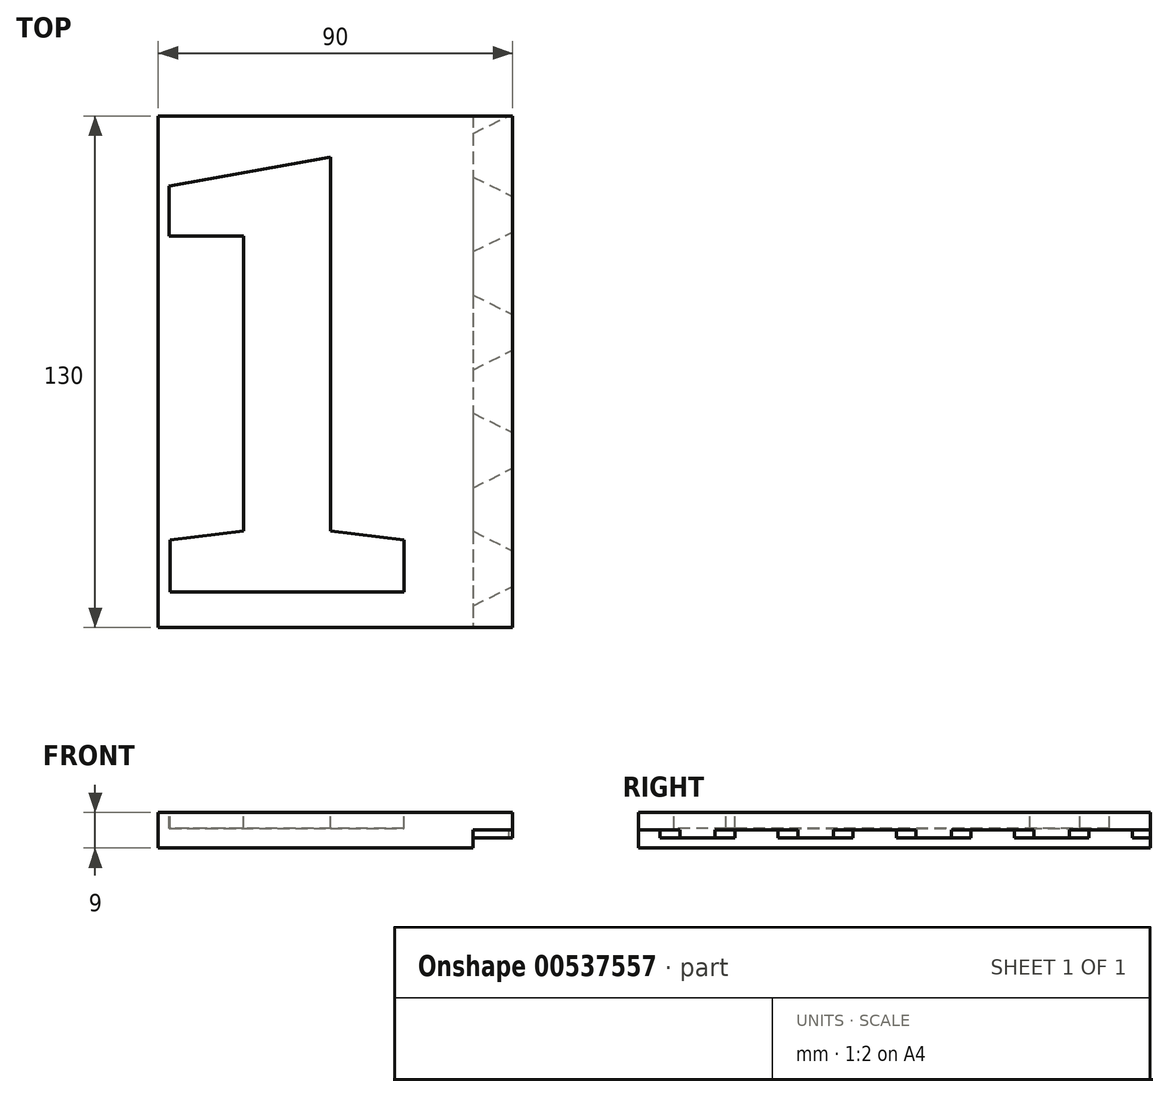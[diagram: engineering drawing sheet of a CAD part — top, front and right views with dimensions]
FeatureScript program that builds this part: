
annotation { "Feature Type Name" : "Feature", "Feature Type Description" : "" }
export const myFeature = defineFeature(function(context is Context, id is Id, definition is map)
    precondition{}
    {
        {
            var Q0;
            Q0=qCreatedBy(makeId("Top.planeOp"),FACE);
            var sketch = newSketch(context, id + "F0", { "sketchPlane" : qUnion([Q0])});
            skLineSegment(sketch, "E0.bottom", {"start": v(45, -65) * mm, "end": v(-45, -65) * mm});
            skLineSegment(sketch, "E0.top", {"start": v(45, 65) * mm, "end": v(-45, 65) * mm});
            skLineSegment(sketch, "E0.left", {"start": v(45, -65) * mm, "end": v(45, 65) * mm});
            skLineSegment(sketch, "E0.right", {"start": v(-45, -65) * mm, "end": v(-45, 65) * mm});
            skPoint(sketch, "E0.middle", {"position": v(0, 0) * mm});
            skSolve(sketch);
        }
        {
            var Q0;
            Q0 = qSketchRegion(id + "F0", true);
            extrude(context, id + "F1", {"entities" : qUnion([Q0]), "depth" : 9 * mm, "offsetDistance" : 25 * mm});
        }
        {
            var Q0;
            Q0=makeQuery(id+"F1.opExtrude","CAP_FACE",FACE,{"disambiguationData":[OSD([sQuery(id+"F0.wireOp",EDGE,"E0.bottom"),sQuery(id+"F0.wireOp",EDGE,"E0.top"),sQuery(id+"F0.wireOp",EDGE,"E0.left"),sQuery(id+"F0.wireOp",EDGE,"E0.right")])],"isStart":false});
            var sketch = newSketch(context, id + "F2", { "sketchPlane" : qUnion([Q0])});
            skLineSegment(sketch, "E1.bottom", {"start": v(-45, 65) * mm, "end": v(35, 65) * mm});
            skLineSegment(sketch, "E1.top", {"start": v(-45, -65) * mm, "end": v(35, -65) * mm});
            skLineSegment(sketch, "E1.left", {"start": v(-45, 65) * mm, "end": v(-45, -65) * mm});
            skLineSegment(sketch, "E1.right", {"start": v(35, 65) * mm, "end": v(35, -65) * mm});
            skText(sketch, "E2", { "text": "1", "fontName": "RobotoSlab-Bold.ttf"});
            skPoint(sketch, "E3", {"position": v(-5, 65) * mm});
            skLineSegment(sketch, "E4", {"start": v(-5, 56) * mm, "end": v(-5, 65) * mm});
            skLineSegment(sketch, "E5", {"start": v(-5, -56) * mm, "end": v(-5, -65) * mm});
            const initialGuessF2  = {"E2": [-0.04697, -0.056, 1, 0, 0.112]};
            skSetInitialGuess(sketch, initialGuessF2);
            skSolve(sketch);
        }
        {
            var Q0;
            Q0=makeQuery(id+"F2.imprint","IMPRINT",FACE,{"disambiguationData":[TD([[makeQuery(id+"F2.imprint","IMPRINT",EDGE,{"derivedFrom":sQuery(id+"F2.wireOp",EDGE,"E2.sketch_text.stroke-0")}),-1.0]])]});
            extrude(context, id + "F3", {"entities" : qUnion([Q0]), "operationType" : NewBodyOperationType.REMOVE, "oppositeDirection" : true, "depth" : 4 * mm, "offsetDistance" : 25 * mm});
        }
        {
            var Q0;
            Q0=makeQuery(id+"F1.opExtrude","CAP_FACE",FACE,{"disambiguationData":[OSD([sQuery(id+"F0.wireOp",EDGE,"E0.bottom"),sQuery(id+"F0.wireOp",EDGE,"E0.top"),sQuery(id+"F0.wireOp",EDGE,"E0.left"),sQuery(id+"F0.wireOp",EDGE,"E0.right")])],"isStart":true});
            var sketch = newSketch(context, id + "F4", { "sketchPlane" : qUnion([Q0])});
            skLineSegment(sketch, "E6.bottom", {"start": v(-45, -65) * mm, "end": v(35, -65) * mm});
            skLineSegment(sketch, "E6.top", {"start": v(-45, 65) * mm, "end": v(35, 65) * mm});
            skLineSegment(sketch, "E6.left", {"start": v(-45, -65) * mm, "end": v(-45, 65) * mm});
            skLineSegment(sketch, "E6.right", {"start": v(35, -65) * mm, "end": v(35, 65) * mm});
            skLineSegment(sketch, "E7", {"start": v(45, -65) * mm, "end": v(45, -45) * mm});
            skLineSegment(sketch, "E8", {"start": v(35, -50) * mm, "end": v(35, -60) * mm});
            skLineSegment(sketch, "E9", {"start": v(45, -65) * mm, "end": v(35, -60) * mm});
            skLineSegment(sketch, "E10", {"start": v(45, -45) * mm, "end": v(35, -50) * mm});
            skLineSegment(sketch, "E11.0.1.0", {"start": v(45, -35) * mm, "end": v(35, -30) * mm});
            skLineSegment(sketch, "E11.0.1.1", {"start": v(45, -35) * mm, "end": v(45, -15) * mm});
            skLineSegment(sketch, "E11.0.1.2", {"start": v(45, -15) * mm, "end": v(35, -20) * mm});
            skLineSegment(sketch, "E11.0.1.3", {"start": v(35, -20) * mm, "end": v(35, -30) * mm});
            skLineSegment(sketch, "E11.0.2.0", {"start": v(45, -5) * mm, "end": v(35, 0) * mm});
            skLineSegment(sketch, "E11.0.2.1", {"start": v(45, -5) * mm, "end": v(45, 15) * mm});
            skLineSegment(sketch, "E11.0.2.2", {"start": v(45, 15) * mm, "end": v(35, 10) * mm});
            skLineSegment(sketch, "E11.0.2.3", {"start": v(35, 10) * mm, "end": v(35, 0) * mm});
            skLineSegment(sketch, "E11.0.3.0", {"start": v(45, 25) * mm, "end": v(35, 30) * mm});
            skLineSegment(sketch, "E11.0.3.1", {"start": v(45, 25) * mm, "end": v(45, 45) * mm});
            skLineSegment(sketch, "E11.0.3.2", {"start": v(45, 45) * mm, "end": v(35, 40) * mm});
            skLineSegment(sketch, "E11.0.3.3", {"start": v(35, 40) * mm, "end": v(35, 30) * mm});
            skLineSegment(sketch, "E11.0.4.0", {"start": v(45, 55) * mm, "end": v(35, 60) * mm});
            skLineSegment(sketch, "E11.0.4.1", {"start": v(45, 55) * mm, "end": v(45, 75) * mm});
            skLineSegment(sketch, "E11.0.4.2", {"start": v(45, 75) * mm, "end": v(35, 70) * mm});
            skLineSegment(sketch, "E11.0.4.3", {"start": v(35, 70) * mm, "end": v(35, 60) * mm});
            skLineSegment(sketch, "E11.direction1", {"start": v(35, -60) * mm, "end": v(55, -60) * mm, "construction": true});
            skLineSegment(sketch, "E11.direction2", {"start": v(35, -60) * mm, "end": v(35, -30) * mm, "construction": true});
            skSolve(sketch);
        }
        {
            var Q0;
            Q0=makeQuery(id+"F4.imprint","IMPRINT",FACE,{"disambiguationData":[TD([[makeQuery(id+"F4.imprint","IMPRINT",EDGE,{"derivedFrom":sQuery(id+"F4.wireOp",EDGE,"E7")}),-1.0]])]});
            var Q1;
            Q1=makeQuery(id+"F4.imprint","IMPRINT",FACE,{"disambiguationData":[TD([[makeQuery(id+"F4.imprint","IMPRINT",EDGE,{"derivedFrom":sQuery(id+"F4.wireOp",EDGE,"E11.0.1.0")}),-1.0]])]});
            var Q2;
            Q2=makeQuery(id+"F4.imprint","IMPRINT",FACE,{"disambiguationData":[TD([[makeQuery(id+"F4.imprint","IMPRINT",EDGE,{"derivedFrom":sQuery(id+"F4.wireOp",EDGE,"E11.0.2.0")}),-1.0]])]});
            var Q3;
            Q3=makeQuery(id+"F4.imprint","IMPRINT",FACE,{"disambiguationData":[TD([[makeQuery(id+"F4.imprint","IMPRINT",EDGE,{"derivedFrom":sQuery(id+"F4.wireOp",EDGE,"E11.0.3.0")}),-1.0]])]});
            var Q4;
            {var subQ0=sQuery(id+"F4.wireOp",EDGE,"E11.0.4.0");Q4=makeQuery(id+"F4.imprint","IMPRINT",FACE,{"disambiguationData":[TD([[makeQuery(id+"F4.imprint","IMPRINT",EDGE,{"derivedFrom":subQ0}),-1.0]])]});}
            extrude(context, id + "F5", {"entities" : qUnion([Q0, Q1, Q2, Q3, Q4]), "operationType" : NewBodyOperationType.REMOVE, "oppositeDirection" : true, "depth" : 4.6 * mm, "offsetDistance" : 25 * mm});
        }
        {
            var Q0;
            {var subQ2=sQuery(id+"F4.wireOp",EDGE,"E11.0.3.2");Q0=makeQuery(id+"F4.imprint","IMPRINT",FACE,{"disambiguationData":[TD([[makeQuery(id+"F4.imprint","IMPRINT",EDGE,{"derivedFrom":subQ2}),-1.0]])]});}
            var Q1;
            {var subQ0=sQuery(id+"F4.wireOp",EDGE,"E11.0.2.2");Q1=makeQuery(id+"F4.imprint","IMPRINT",FACE,{"disambiguationData":[TD([[makeQuery(id+"F4.imprint","IMPRINT",EDGE,{"derivedFrom":subQ0}),-1.0]])]});}
            var Q2;
            {var subQ0=sQuery(id+"F4.wireOp",EDGE,"E11.0.1.2");Q2=makeQuery(id+"F4.imprint","IMPRINT",FACE,{"disambiguationData":[TD([[makeQuery(id+"F4.imprint","IMPRINT",EDGE,{"derivedFrom":subQ0}),-1.0]])]});}
            var Q3;
            {var subQ0=sQuery(id+"F4.wireOp",EDGE,"E10");Q3=makeQuery(id+"F4.imprint","IMPRINT",FACE,{"disambiguationData":[TD([[makeQuery(id+"F4.imprint","IMPRINT",EDGE,{"derivedFrom":subQ0}),-1.0]])]});}
            var Q4;
            {var subQ3=sQuery(id+"F4.wireOp",EDGE,"E9");Q4=makeQuery(id+"F4.imprint","IMPRINT",FACE,{"disambiguationData":[TD([[makeQuery(id+"F4.imprint","IMPRINT",EDGE,{"derivedFrom":subQ3}),1.0]])]});}
            extrude(context, id + "F6", {"entities" : qUnion([Q0, Q1, Q2, Q3, Q4]), "operationType" : NewBodyOperationType.REMOVE, "oppositeDirection" : true, "depth" : 2.6 * mm, "offsetDistance" : 25 * mm});
        }
        {
            var Q0;
            Q0=makeQuery(id+"F6.boolean.opBoolean","COPY",FACE,{"derivedFrom":makeQuery(id+"F6.opExtrude","CAP_FACE",FACE,{"disambiguationData":[OSD([sQuery(id+"F0.wireOp",EDGE,"E0.left"),sQuery(id+"F4.wireOp",EDGE,"E6.right"),sQuery(id+"F4.wireOp",EDGE,"E11.0.3.2"),sQuery(id+"F4.wireOp",EDGE,"E11.0.4.0")])],"isStart":false})});
            var sketch = newSketch(context, id + "F7", { "sketchPlane" : qUnion([Q0])});
            skLineSegment(sketch, "E12", {"start": v(35, 60) * mm, "end": v(35, 59.5) * mm});
            skLineSegment(sketch, "E13", {"start": v(35, 59.5) * mm, "end": v(45, 54.5) * mm});
            skLineSegment(sketch, "E14", {"start": v(45, 54.5) * mm, "end": v(45, 55) * mm});
            skLineSegment(sketch, "E15", {"start": v(45, 55) * mm, "end": v(35, 60) * mm});
            skLineSegment(sketch, "E16", {"start": v(35, 40) * mm, "end": v(35, 40.5) * mm});
            skLineSegment(sketch, "E17", {"start": v(35, 40.5) * mm, "end": v(45, 45.5) * mm});
            skLineSegment(sketch, "E18", {"start": v(45, 45.5) * mm, "end": v(45, 45) * mm});
            skLineSegment(sketch, "E19", {"start": v(35, 40) * mm, "end": v(45, 45) * mm});
            skLineSegment(sketch, "E20.0.1.0", {"start": v(45, 25) * mm, "end": v(35, 30) * mm});
            skLineSegment(sketch, "E20.0.1.1", {"start": v(35, 29.5) * mm, "end": v(45, 24.5) * mm});
            skLineSegment(sketch, "E20.0.1.2", {"start": v(45, 24.5) * mm, "end": v(45, 25) * mm});
            skLineSegment(sketch, "E20.0.1.3", {"start": v(35, 30) * mm, "end": v(35, 29.5) * mm});
            skLineSegment(sketch, "E20.0.1.4", {"start": v(35, 10.5) * mm, "end": v(45, 15.5) * mm});
            skLineSegment(sketch, "E20.0.1.5", {"start": v(35, 10) * mm, "end": v(45, 15) * mm});
            skLineSegment(sketch, "E20.0.1.6", {"start": v(35, 10) * mm, "end": v(35, 10.5) * mm});
            skLineSegment(sketch, "E20.0.1.7", {"start": v(45, 15.5) * mm, "end": v(45, 15) * mm});
            skLineSegment(sketch, "E20.0.2.0", {"start": v(45, -5) * mm, "end": v(35, 0) * mm});
            skLineSegment(sketch, "E20.0.2.1", {"start": v(35, -0.5) * mm, "end": v(45, -5.5) * mm});
            skLineSegment(sketch, "E20.0.2.2", {"start": v(45, -5.5) * mm, "end": v(45, -5) * mm});
            skLineSegment(sketch, "E20.0.2.3", {"start": v(35, 0) * mm, "end": v(35, -0.5) * mm});
            skLineSegment(sketch, "E20.0.2.4", {"start": v(35, -19.5) * mm, "end": v(45, -14.5) * mm});
            skLineSegment(sketch, "E20.0.2.5", {"start": v(35, -20) * mm, "end": v(45, -15) * mm});
            skLineSegment(sketch, "E20.0.2.6", {"start": v(35, -20) * mm, "end": v(35, -19.5) * mm});
            skLineSegment(sketch, "E20.0.2.7", {"start": v(45, -14.5) * mm, "end": v(45, -15) * mm});
            skLineSegment(sketch, "E20.0.3.0", {"start": v(45, -35) * mm, "end": v(35, -30) * mm});
            skLineSegment(sketch, "E20.0.3.1", {"start": v(35, -30.5) * mm, "end": v(45, -35.5) * mm});
            skLineSegment(sketch, "E20.0.3.2", {"start": v(45, -35.5) * mm, "end": v(45, -35) * mm});
            skLineSegment(sketch, "E20.0.3.3", {"start": v(35, -30) * mm, "end": v(35, -30.5) * mm});
            skLineSegment(sketch, "E20.0.3.4", {"start": v(35, -49.5) * mm, "end": v(45, -44.5) * mm});
            skLineSegment(sketch, "E20.0.3.5", {"start": v(35, -50) * mm, "end": v(45, -45) * mm});
            skLineSegment(sketch, "E20.0.3.6", {"start": v(35, -50) * mm, "end": v(35, -49.5) * mm});
            skLineSegment(sketch, "E20.0.3.7", {"start": v(45, -44.5) * mm, "end": v(45, -45) * mm});
            skLineSegment(sketch, "E20.0.4.0", {"start": v(45, -65) * mm, "end": v(35, -60) * mm});
            skLineSegment(sketch, "E20.0.4.1", {"start": v(35, -60.5) * mm, "end": v(45, -65.5) * mm});
            skLineSegment(sketch, "E20.0.4.2", {"start": v(45, -65.5) * mm, "end": v(45, -65) * mm});
            skLineSegment(sketch, "E20.0.4.3", {"start": v(35, -60) * mm, "end": v(35, -60.5) * mm});
            skLineSegment(sketch, "E20.0.4.4", {"start": v(35, -79.5) * mm, "end": v(45, -74.5) * mm});
            skLineSegment(sketch, "E20.0.4.5", {"start": v(35, -80) * mm, "end": v(45, -75) * mm});
            skLineSegment(sketch, "E20.0.4.6", {"start": v(35, -80) * mm, "end": v(35, -79.5) * mm});
            skLineSegment(sketch, "E20.0.4.7", {"start": v(45, -74.5) * mm, "end": v(45, -75) * mm});
            skLineSegment(sketch, "E20.direction1", {"start": v(35, 60) * mm, "end": v(60, 60) * mm, "construction": true});
            skLineSegment(sketch, "E20.direction2", {"start": v(35, 60) * mm, "end": v(35, 30) * mm, "construction": true});
            skSolve(sketch);
        }
        {
            var Q0;
            Q0 = qSketchRegion(id + "F7", true);
            extrude(context, id + "F8", {"entities" : qUnion([Q0]), "operationType" : NewBodyOperationType.REMOVE, "oppositeDirection" : true, "depth" : 2 * mm, "offsetDistance" : 25 * mm});
        }
    });
